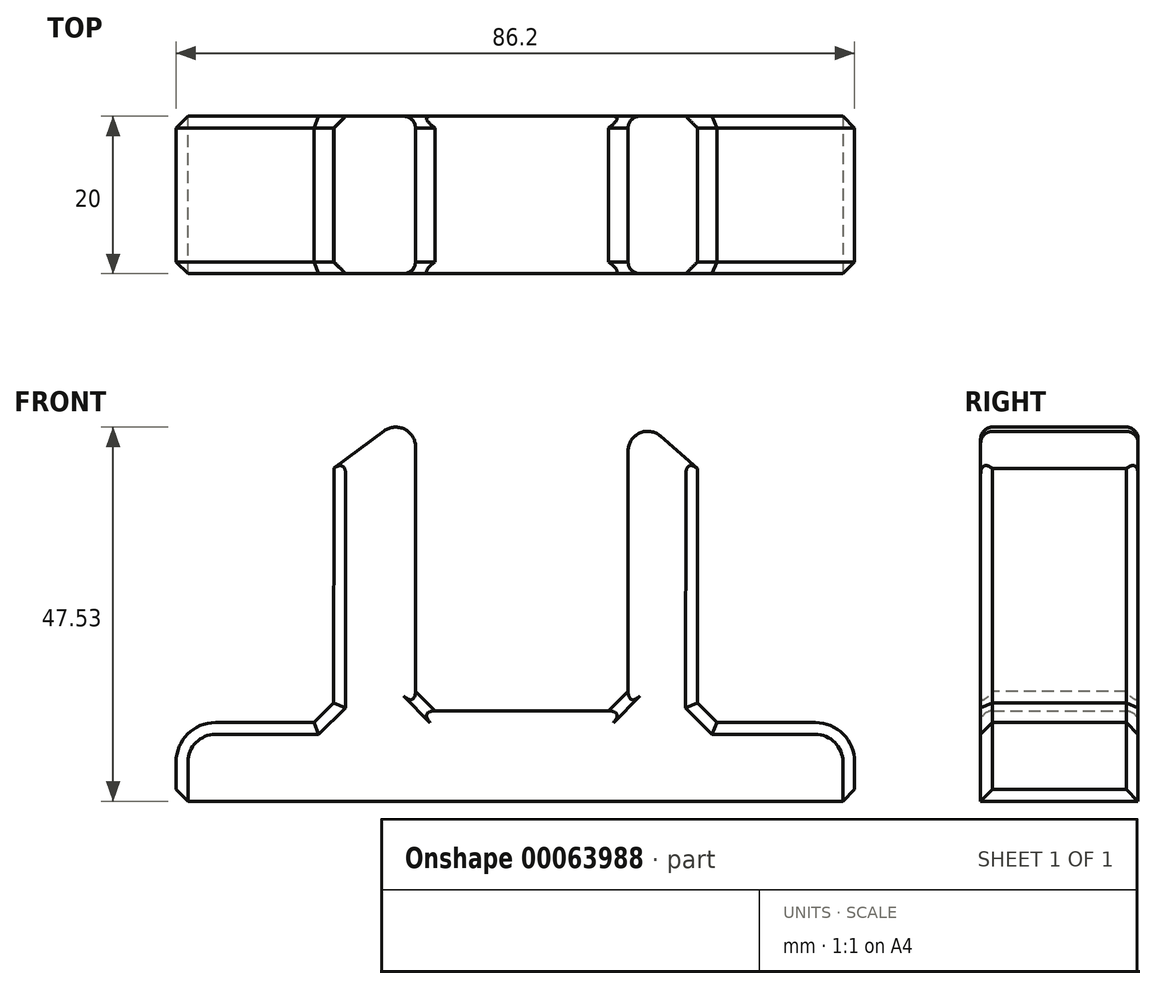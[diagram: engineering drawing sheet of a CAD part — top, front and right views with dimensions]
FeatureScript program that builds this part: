
annotation { "Feature Type Name" : "Feature", "Feature Type Description" : "" }
export const myFeature = defineFeature(function(context is Context, id is Id, definition is map)
    precondition{}
    {
        {
            var Q0;
            Q0=qCreatedBy(makeId("Front.planeOp"),FACE);
            var sketch = newSketch(context, id + "F0", { "sketchPlane" : qUnion([Q0])});
            skLineSegment(sketch, "E0.rect.bottom", {"start": v(43.1, 0) * mm, "end": v(-43.1, 0) * mm});
            skLineSegment(sketch, "E0.rect.top", {"start": v(43.1, 10) * mm, "end": v(23.1, 10) * mm});
            skLineSegment(sketch, "E0.rect.left", {"start": v(43.1, 0) * mm, "end": v(43.1, 10) * mm});
            skLineSegment(sketch, "E0.rect.right", {"start": v(-43.1, 0) * mm, "end": v(-43.1, 10) * mm});
            skPoint(sketch, "E0.rect.middle", {"position": v(0, 5) * mm});
            skLineSegment(sketch, "E1.left", {"start": v(-23.06, 42.34) * mm, "end": v(-23.1, 10) * mm});
            skLineSegment(sketch, "E1.right", {"start": v(23.14, 42.27) * mm, "end": v(23.1, 10) * mm});
            skLineSegment(sketch, "E2", {"start": v(-12.7, 49.99) * mm, "end": v(-12.7, 11.49) * mm});
            skLineSegment(sketch, "E3", {"start": v(-12.7, 11.49) * mm, "end": v(14.3, 11.49) * mm});
            skLineSegment(sketch, "E4", {"start": v(14.3, 11.49) * mm, "end": v(14.3, 50.01) * mm});
            skLineSegment(sketch, "E5.trimOffspring", {"start": v(-23.1, 10) * mm, "end": v(-43.1, 10) * mm});
            skPoint(sketch, "E1.bottom.end.orphan", {"position": v(-12.7, 90.4) * mm});
            skPoint(sketch, "E6.trimOffspring.start.orphan", {"position": v(14.3, 90.4) * mm});
            skLineSegment(sketch, "E7", {"start": v(-12.7, 49.99) * mm, "end": v(-23.06, 42.34) * mm});
            skLineSegment(sketch, "E8", {"start": v(23.14, 42.27) * mm, "end": v(14.3, 50.01) * mm});
            skSolve(sketch);
        }
        {
            var Q0;
            Q0=makeQuery(id+"F0.imprint","IMPRINT",FACE,{"disambiguationData":[TD([[makeQuery(id+"F0.imprint","IMPRINT",EDGE,{"derivedFrom":sQuery(id+"F0.wireOp",EDGE,"E0.rect.bottom")}),-1.0]])]});
            extrude(context, id + "F1", {"entities" : qUnion([Q0]), "depth" : 20 * mm});
        }
        {
            var Q0;
            Q0=makeQuery(id+"F1.opExtrude","SWEPT_EDGE",EDGE,{"disambiguationData":[OSD([sQuery(id+"F0.wireOp",EDGE,"E0.rect.top"),sQuery(id+"F0.wireOp",EDGE,"E0.rect.left")])]});
            fillet(context, id + "F2", {"entities" : qUnion([Q0]), "radius" : 5 * mm, "tangentPropagation" : true, "allowEdgeOverflow" : false});
        }
        {
            var Q0;
            Q0=makeQuery(id+"F1.opExtrude","SWEPT_EDGE",EDGE,{"disambiguationData":[OSD([sQuery(id+"F0.wireOp",EDGE,"E0.rect.right"),sQuery(id+"F0.wireOp",EDGE,"E5.trimOffspring")])]});
            fillet(context, id + "F3", {"entities" : qUnion([Q0]), "radius" : 5 * mm, "tangentPropagation" : true, "allowEdgeOverflow" : false});
        }
        {
            var Q0;
            Q0=makeQuery(id+"F1.opExtrude","SWEPT_EDGE",EDGE,{"disambiguationData":[OSD([sQuery(id+"F0.wireOp",EDGE,"E1.left"),sQuery(id+"F0.wireOp",EDGE,"E5.trimOffspring")])]});
            var Q1;
            Q1=makeQuery(id+"F1.opExtrude","SWEPT_EDGE",EDGE,{"disambiguationData":[OSD([sQuery(id+"F0.wireOp",EDGE,"E0.rect.top"),sQuery(id+"F0.wireOp",EDGE,"E1.right")])]});
            chamfer(context, id + "F4", {"entities" : qUnion([Q0, Q1]), "width" : 2.5 * mm, "tangentPropagation" : true});
        }
        {
            var Q0;
            Q0=makeQuery(id+"F1.opExtrude","SWEPT_EDGE",EDGE,{"disambiguationData":[OSD([sQuery(id+"F0.wireOp",EDGE,"E0.rect.bottom"),sQuery(id+"F0.wireOp",EDGE,"E0.rect.right")])]});
            chamfer(context, id + "F5", {"entities" : qUnion([Q0]), "width" : 1.5 * mm, "tangentPropagation" : true});
        }
        {
            var Q0;
            Q0=makeQuery(id+"F1.opExtrude","SWEPT_EDGE",EDGE,{"disambiguationData":[OSD([sQuery(id+"F0.wireOp",EDGE,"E0.rect.bottom"),sQuery(id+"F0.wireOp",EDGE,"E0.rect.left")])]});
            chamfer(context, id + "F6", {"entities" : qUnion([Q0]), "width" : 1.5 * mm, "tangentPropagation" : true});
        }
        {
            var Q0;
            Q0=makeQuery(id+"F1.opExtrude","SWEPT_EDGE",EDGE,{"disambiguationData":[OSD([sQuery(id+"F0.wireOp",EDGE,"E2"),sQuery(id+"F0.wireOp",EDGE,"E3")])]});
            chamfer(context, id + "F7", {"entities" : qUnion([Q0]), "width" : 2.5 * mm, "tangentPropagation" : true});
        }
        {
            var Q0;
            Q0=makeQuery(id+"F1.opExtrude","SWEPT_EDGE",EDGE,{"disambiguationData":[OSD([sQuery(id+"F0.wireOp",EDGE,"E3"),sQuery(id+"F0.wireOp",EDGE,"E4")])]});
            chamfer(context, id + "F8", {"entities" : qUnion([Q0]), "width" : 2.5 * mm, "tangentPropagation" : true});
        }
        {
            var Q0;
            Q0=makeQuery(id+"F1.opExtrude","SWEPT_EDGE",EDGE,{"disambiguationData":[OSD([sQuery(id+"F0.wireOp",EDGE,"E2"),sQuery(id+"F0.wireOp",EDGE,"E7")])]});
            fillet(context, id + "F9", {"entities" : qUnion([Q0]), "radius" : 2.5 * mm, "tangentPropagation" : true, "allowEdgeOverflow" : false});
        }
        {
            var Q0;
            Q0=makeQuery(id+"F1.opExtrude","SWEPT_EDGE",EDGE,{"disambiguationData":[OSD([sQuery(id+"F0.wireOp",EDGE,"E4"),sQuery(id+"F0.wireOp",EDGE,"E8")])]});
            fillet(context, id + "F10", {"entities" : qUnion([Q0]), "radius" : 2.5 * mm, "tangentPropagation" : true, "allowEdgeOverflow" : false});
        }
        {
            var Q0;
            Q0=makeQuery(id+"F1.opExtrude","CAP_EDGE",EDGE,{"disambiguationData":[OSD([sQuery(id+"F0.wireOp",EDGE,"E1.left")])],"isStart":false});
            chamfer(context, id + "F11", {"entities" : qUnion([Q0]), "width" : 1.5 * mm, "tangentPropagation" : true});
        }
        {
            var Q0;
            Q0=makeQuery(id+"F1.opExtrude","CAP_EDGE",EDGE,{"disambiguationData":[OSD([sQuery(id+"F0.wireOp",EDGE,"E1.right")])],"isStart":true});
            var Q1;
            Q1=makeQuery(id+"F1.opExtrude","CAP_EDGE",EDGE,{"disambiguationData":[OSD([sQuery(id+"F0.wireOp",EDGE,"E1.left")])],"isStart":true});
            var Q2;
            Q2=makeQuery(id+"F1.opExtrude","CAP_EDGE",EDGE,{"disambiguationData":[OSD([sQuery(id+"F0.wireOp",EDGE,"E1.right")])],"isStart":false});
            chamfer(context, id + "F12", {"entities" : qUnion([Q0, Q1, Q2]), "width" : 1.5 * mm, "tangentPropagation" : true});
        }
        {
            var Q0;
            Q0=makeQuery(id+"F1.opExtrude","CAP_EDGE",EDGE,{"disambiguationData":[OSD([sQuery(id+"F0.wireOp",EDGE,"E2")])],"isStart":false});
            var Q1;
            Q1=makeQuery(id+"F1.opExtrude","CAP_EDGE",EDGE,{"disambiguationData":[OSD([sQuery(id+"F0.wireOp",EDGE,"E4")])],"isStart":false});
            fillet(context, id + "F13", {"entities" : qUnion([Q0, Q1]), "radius" : 1.5 * mm, "tangentPropagation" : true, "allowEdgeOverflow" : false});
        }
        {
            var Q0;
            {var subQ0=sQuery(id+"F0.wireOp",EDGE,"E1.right");var subQ1=sQuery(id+"F0.wireOp",EDGE,"E0.rect.top");Q0=makeQuery(id+"F4.opChamfer","BLEND_EDGE",EDGE,{"blendedFrom":[makeQuery(id+"F1.opExtrude","SWEPT_EDGE",EDGE,{"disambiguationData":[OSD([subQ1,subQ0])]}),makeQuery(id+"F1.opExtrude","CAP_FACE",FACE,{"disambiguationData":[OSD([sQuery(id+"F0.wireOp",EDGE,"E0.rect.bottom"),subQ1,sQuery(id+"F0.wireOp",EDGE,"E0.rect.left"),sQuery(id+"F0.wireOp",EDGE,"E0.rect.right"),sQuery(id+"F0.wireOp",EDGE,"E1.left"),subQ0,sQuery(id+"F0.wireOp",EDGE,"E2"),sQuery(id+"F0.wireOp",EDGE,"E3"),sQuery(id+"F0.wireOp",EDGE,"E4"),sQuery(id+"F0.wireOp",EDGE,"E5.trimOffspring"),sQuery(id+"F0.wireOp",EDGE,"E7"),sQuery(id+"F0.wireOp",EDGE,"E8")])],"isStart":false})],"blendedInto":[makeQuery(id+"F1.opExtrude","CAP_FACE",FACE,{"disambiguationData":[OSD([sQuery(id+"F0.wireOp",EDGE,"E0.rect.bottom"),subQ1,sQuery(id+"F0.wireOp",EDGE,"E0.rect.left"),sQuery(id+"F0.wireOp",EDGE,"E0.rect.right"),sQuery(id+"F0.wireOp",EDGE,"E1.left"),subQ0,sQuery(id+"F0.wireOp",EDGE,"E2"),sQuery(id+"F0.wireOp",EDGE,"E3"),sQuery(id+"F0.wireOp",EDGE,"E4"),sQuery(id+"F0.wireOp",EDGE,"E5.trimOffspring"),sQuery(id+"F0.wireOp",EDGE,"E7"),sQuery(id+"F0.wireOp",EDGE,"E8")])],"isStart":false})]});}
            chamfer(context, id + "F14", {"entities" : qUnion([Q0]), "width" : 1.5 * mm, "tangentPropagation" : true});
        }
        {
            var Q0;
            Q0=makeQuery(id+"F1.opExtrude","CAP_EDGE",EDGE,{"disambiguationData":[OSD([sQuery(id+"F0.wireOp",EDGE,"E0.rect.top")])],"isStart":false});
            var Q1;
            Q1=makeQuery(id+"F1.opExtrude","CAP_EDGE",EDGE,{"disambiguationData":[OSD([sQuery(id+"F0.wireOp",EDGE,"E0.rect.top")])],"isStart":true});
            var Q2;
            {var subQ0=sQuery(id+"F0.wireOp",EDGE,"E1.right");var subQ1=sQuery(id+"F0.wireOp",EDGE,"E0.rect.top");Q2=makeQuery(id+"F4.opChamfer","BLEND_EDGE",EDGE,{"blendedFrom":[makeQuery(id+"F1.opExtrude","SWEPT_EDGE",EDGE,{"disambiguationData":[OSD([subQ1,subQ0])]}),makeQuery(id+"F1.opExtrude","CAP_FACE",FACE,{"disambiguationData":[OSD([sQuery(id+"F0.wireOp",EDGE,"E0.rect.bottom"),subQ1,sQuery(id+"F0.wireOp",EDGE,"E0.rect.left"),sQuery(id+"F0.wireOp",EDGE,"E0.rect.right"),sQuery(id+"F0.wireOp",EDGE,"E1.left"),subQ0,sQuery(id+"F0.wireOp",EDGE,"E2"),sQuery(id+"F0.wireOp",EDGE,"E3"),sQuery(id+"F0.wireOp",EDGE,"E4"),sQuery(id+"F0.wireOp",EDGE,"E5.trimOffspring"),sQuery(id+"F0.wireOp",EDGE,"E7"),sQuery(id+"F0.wireOp",EDGE,"E8")])],"isStart":true})],"blendedInto":[makeQuery(id+"F1.opExtrude","CAP_FACE",FACE,{"disambiguationData":[OSD([sQuery(id+"F0.wireOp",EDGE,"E0.rect.bottom"),subQ1,sQuery(id+"F0.wireOp",EDGE,"E0.rect.left"),sQuery(id+"F0.wireOp",EDGE,"E0.rect.right"),sQuery(id+"F0.wireOp",EDGE,"E1.left"),subQ0,sQuery(id+"F0.wireOp",EDGE,"E2"),sQuery(id+"F0.wireOp",EDGE,"E3"),sQuery(id+"F0.wireOp",EDGE,"E4"),sQuery(id+"F0.wireOp",EDGE,"E5.trimOffspring"),sQuery(id+"F0.wireOp",EDGE,"E7"),sQuery(id+"F0.wireOp",EDGE,"E8")])],"isStart":true})]});}
            var Q3;
            {var subQ0=sQuery(id+"F0.wireOp",EDGE,"E4");var subQ1=sQuery(id+"F0.wireOp",EDGE,"E3");Q3=makeQuery(id+"F8.opChamfer","BLEND_EDGE",EDGE,{"blendedFrom":[makeQuery(id+"F1.opExtrude","SWEPT_EDGE",EDGE,{"disambiguationData":[OSD([subQ1,subQ0])]}),makeQuery(id+"F1.opExtrude","CAP_FACE",FACE,{"disambiguationData":[OSD([sQuery(id+"F0.wireOp",EDGE,"E0.rect.bottom"),sQuery(id+"F0.wireOp",EDGE,"E0.rect.top"),sQuery(id+"F0.wireOp",EDGE,"E0.rect.left"),sQuery(id+"F0.wireOp",EDGE,"E0.rect.right"),sQuery(id+"F0.wireOp",EDGE,"E1.left"),sQuery(id+"F0.wireOp",EDGE,"E1.right"),sQuery(id+"F0.wireOp",EDGE,"E2"),subQ1,subQ0,sQuery(id+"F0.wireOp",EDGE,"E5.trimOffspring"),sQuery(id+"F0.wireOp",EDGE,"E7"),sQuery(id+"F0.wireOp",EDGE,"E8")])],"isStart":false})],"blendedInto":[makeQuery(id+"F1.opExtrude","CAP_FACE",FACE,{"disambiguationData":[OSD([sQuery(id+"F0.wireOp",EDGE,"E0.rect.bottom"),sQuery(id+"F0.wireOp",EDGE,"E0.rect.top"),sQuery(id+"F0.wireOp",EDGE,"E0.rect.left"),sQuery(id+"F0.wireOp",EDGE,"E0.rect.right"),sQuery(id+"F0.wireOp",EDGE,"E1.left"),sQuery(id+"F0.wireOp",EDGE,"E1.right"),sQuery(id+"F0.wireOp",EDGE,"E2"),subQ1,subQ0,sQuery(id+"F0.wireOp",EDGE,"E5.trimOffspring"),sQuery(id+"F0.wireOp",EDGE,"E7"),sQuery(id+"F0.wireOp",EDGE,"E8")])],"isStart":false})]});}
            var Q4;
            {var subQ0=sQuery(id+"F0.wireOp",EDGE,"E3");var subQ1=sQuery(id+"F0.wireOp",EDGE,"E2");Q4=makeQuery(id+"F7.opChamfer","BLEND_EDGE",EDGE,{"blendedFrom":[makeQuery(id+"F1.opExtrude","SWEPT_EDGE",EDGE,{"disambiguationData":[OSD([subQ1,subQ0])]}),makeQuery(id+"F1.opExtrude","CAP_FACE",FACE,{"disambiguationData":[OSD([sQuery(id+"F0.wireOp",EDGE,"E0.rect.bottom"),sQuery(id+"F0.wireOp",EDGE,"E0.rect.top"),sQuery(id+"F0.wireOp",EDGE,"E0.rect.left"),sQuery(id+"F0.wireOp",EDGE,"E0.rect.right"),sQuery(id+"F0.wireOp",EDGE,"E1.left"),sQuery(id+"F0.wireOp",EDGE,"E1.right"),subQ1,subQ0,sQuery(id+"F0.wireOp",EDGE,"E4"),sQuery(id+"F0.wireOp",EDGE,"E5.trimOffspring"),sQuery(id+"F0.wireOp",EDGE,"E7"),sQuery(id+"F0.wireOp",EDGE,"E8")])],"isStart":false})],"blendedInto":[makeQuery(id+"F1.opExtrude","CAP_FACE",FACE,{"disambiguationData":[OSD([sQuery(id+"F0.wireOp",EDGE,"E0.rect.bottom"),sQuery(id+"F0.wireOp",EDGE,"E0.rect.top"),sQuery(id+"F0.wireOp",EDGE,"E0.rect.left"),sQuery(id+"F0.wireOp",EDGE,"E0.rect.right"),sQuery(id+"F0.wireOp",EDGE,"E1.left"),sQuery(id+"F0.wireOp",EDGE,"E1.right"),subQ1,subQ0,sQuery(id+"F0.wireOp",EDGE,"E4"),sQuery(id+"F0.wireOp",EDGE,"E5.trimOffspring"),sQuery(id+"F0.wireOp",EDGE,"E7"),sQuery(id+"F0.wireOp",EDGE,"E8")])],"isStart":false})]});}
            var Q5;
            {var subQ0=sQuery(id+"F0.wireOp",EDGE,"E5.trimOffspring");var subQ1=sQuery(id+"F0.wireOp",EDGE,"E1.left");Q5=makeQuery(id+"F4.opChamfer","BLEND_EDGE",EDGE,{"blendedFrom":[makeQuery(id+"F1.opExtrude","SWEPT_EDGE",EDGE,{"disambiguationData":[OSD([subQ1,subQ0])]}),makeQuery(id+"F1.opExtrude","CAP_FACE",FACE,{"disambiguationData":[OSD([sQuery(id+"F0.wireOp",EDGE,"E0.rect.bottom"),sQuery(id+"F0.wireOp",EDGE,"E0.rect.top"),sQuery(id+"F0.wireOp",EDGE,"E0.rect.left"),sQuery(id+"F0.wireOp",EDGE,"E0.rect.right"),subQ1,sQuery(id+"F0.wireOp",EDGE,"E1.right"),sQuery(id+"F0.wireOp",EDGE,"E2"),sQuery(id+"F0.wireOp",EDGE,"E3"),sQuery(id+"F0.wireOp",EDGE,"E4"),subQ0,sQuery(id+"F0.wireOp",EDGE,"E7"),sQuery(id+"F0.wireOp",EDGE,"E8")])],"isStart":false})],"blendedInto":[makeQuery(id+"F1.opExtrude","CAP_FACE",FACE,{"disambiguationData":[OSD([sQuery(id+"F0.wireOp",EDGE,"E0.rect.bottom"),sQuery(id+"F0.wireOp",EDGE,"E0.rect.top"),sQuery(id+"F0.wireOp",EDGE,"E0.rect.left"),sQuery(id+"F0.wireOp",EDGE,"E0.rect.right"),subQ1,sQuery(id+"F0.wireOp",EDGE,"E1.right"),sQuery(id+"F0.wireOp",EDGE,"E2"),sQuery(id+"F0.wireOp",EDGE,"E3"),sQuery(id+"F0.wireOp",EDGE,"E4"),subQ0,sQuery(id+"F0.wireOp",EDGE,"E7"),sQuery(id+"F0.wireOp",EDGE,"E8")])],"isStart":false})]});}
            var Q6;
            Q6=makeQuery(id+"F1.opExtrude","CAP_EDGE",EDGE,{"disambiguationData":[OSD([sQuery(id+"F0.wireOp",EDGE,"E5.trimOffspring")])],"isStart":false});
            var Q7;
            {var subQ0=sQuery(id+"F0.wireOp",EDGE,"E4");var subQ1=sQuery(id+"F0.wireOp",EDGE,"E3");Q7=makeQuery(id+"F8.opChamfer","BLEND_EDGE",EDGE,{"blendedFrom":[makeQuery(id+"F1.opExtrude","SWEPT_EDGE",EDGE,{"disambiguationData":[OSD([subQ1,subQ0])]}),makeQuery(id+"F1.opExtrude","CAP_FACE",FACE,{"disambiguationData":[OSD([sQuery(id+"F0.wireOp",EDGE,"E0.rect.bottom"),sQuery(id+"F0.wireOp",EDGE,"E0.rect.top"),sQuery(id+"F0.wireOp",EDGE,"E0.rect.left"),sQuery(id+"F0.wireOp",EDGE,"E0.rect.right"),sQuery(id+"F0.wireOp",EDGE,"E1.left"),sQuery(id+"F0.wireOp",EDGE,"E1.right"),sQuery(id+"F0.wireOp",EDGE,"E2"),subQ1,subQ0,sQuery(id+"F0.wireOp",EDGE,"E5.trimOffspring"),sQuery(id+"F0.wireOp",EDGE,"E7"),sQuery(id+"F0.wireOp",EDGE,"E8")])],"isStart":true})],"blendedInto":[makeQuery(id+"F1.opExtrude","CAP_FACE",FACE,{"disambiguationData":[OSD([sQuery(id+"F0.wireOp",EDGE,"E0.rect.bottom"),sQuery(id+"F0.wireOp",EDGE,"E0.rect.top"),sQuery(id+"F0.wireOp",EDGE,"E0.rect.left"),sQuery(id+"F0.wireOp",EDGE,"E0.rect.right"),sQuery(id+"F0.wireOp",EDGE,"E1.left"),sQuery(id+"F0.wireOp",EDGE,"E1.right"),sQuery(id+"F0.wireOp",EDGE,"E2"),subQ1,subQ0,sQuery(id+"F0.wireOp",EDGE,"E5.trimOffspring"),sQuery(id+"F0.wireOp",EDGE,"E7"),sQuery(id+"F0.wireOp",EDGE,"E8")])],"isStart":true})]});}
            var Q8;
            {var subQ0=sQuery(id+"F0.wireOp",EDGE,"E3");var subQ1=sQuery(id+"F0.wireOp",EDGE,"E2");Q8=makeQuery(id+"F7.opChamfer","BLEND_EDGE",EDGE,{"blendedFrom":[makeQuery(id+"F1.opExtrude","SWEPT_EDGE",EDGE,{"disambiguationData":[OSD([subQ1,subQ0])]}),makeQuery(id+"F1.opExtrude","CAP_FACE",FACE,{"disambiguationData":[OSD([sQuery(id+"F0.wireOp",EDGE,"E0.rect.bottom"),sQuery(id+"F0.wireOp",EDGE,"E0.rect.top"),sQuery(id+"F0.wireOp",EDGE,"E0.rect.left"),sQuery(id+"F0.wireOp",EDGE,"E0.rect.right"),sQuery(id+"F0.wireOp",EDGE,"E1.left"),sQuery(id+"F0.wireOp",EDGE,"E1.right"),subQ1,subQ0,sQuery(id+"F0.wireOp",EDGE,"E4"),sQuery(id+"F0.wireOp",EDGE,"E5.trimOffspring"),sQuery(id+"F0.wireOp",EDGE,"E7"),sQuery(id+"F0.wireOp",EDGE,"E8")])],"isStart":true})],"blendedInto":[makeQuery(id+"F1.opExtrude","CAP_FACE",FACE,{"disambiguationData":[OSD([sQuery(id+"F0.wireOp",EDGE,"E0.rect.bottom"),sQuery(id+"F0.wireOp",EDGE,"E0.rect.top"),sQuery(id+"F0.wireOp",EDGE,"E0.rect.left"),sQuery(id+"F0.wireOp",EDGE,"E0.rect.right"),sQuery(id+"F0.wireOp",EDGE,"E1.left"),sQuery(id+"F0.wireOp",EDGE,"E1.right"),subQ1,subQ0,sQuery(id+"F0.wireOp",EDGE,"E4"),sQuery(id+"F0.wireOp",EDGE,"E5.trimOffspring"),sQuery(id+"F0.wireOp",EDGE,"E7"),sQuery(id+"F0.wireOp",EDGE,"E8")])],"isStart":true})]});}
            var Q9;
            {var subQ0=sQuery(id+"F0.wireOp",EDGE,"E5.trimOffspring");var subQ1=sQuery(id+"F0.wireOp",EDGE,"E1.left");Q9=makeQuery(id+"F4.opChamfer","BLEND_EDGE",EDGE,{"blendedFrom":[makeQuery(id+"F1.opExtrude","SWEPT_EDGE",EDGE,{"disambiguationData":[OSD([subQ1,subQ0])]}),makeQuery(id+"F1.opExtrude","CAP_FACE",FACE,{"disambiguationData":[OSD([sQuery(id+"F0.wireOp",EDGE,"E0.rect.bottom"),sQuery(id+"F0.wireOp",EDGE,"E0.rect.top"),sQuery(id+"F0.wireOp",EDGE,"E0.rect.left"),sQuery(id+"F0.wireOp",EDGE,"E0.rect.right"),subQ1,sQuery(id+"F0.wireOp",EDGE,"E1.right"),sQuery(id+"F0.wireOp",EDGE,"E2"),sQuery(id+"F0.wireOp",EDGE,"E3"),sQuery(id+"F0.wireOp",EDGE,"E4"),subQ0,sQuery(id+"F0.wireOp",EDGE,"E7"),sQuery(id+"F0.wireOp",EDGE,"E8")])],"isStart":true})],"blendedInto":[makeQuery(id+"F1.opExtrude","CAP_FACE",FACE,{"disambiguationData":[OSD([sQuery(id+"F0.wireOp",EDGE,"E0.rect.bottom"),sQuery(id+"F0.wireOp",EDGE,"E0.rect.top"),sQuery(id+"F0.wireOp",EDGE,"E0.rect.left"),sQuery(id+"F0.wireOp",EDGE,"E0.rect.right"),subQ1,sQuery(id+"F0.wireOp",EDGE,"E1.right"),sQuery(id+"F0.wireOp",EDGE,"E2"),sQuery(id+"F0.wireOp",EDGE,"E3"),sQuery(id+"F0.wireOp",EDGE,"E4"),subQ0,sQuery(id+"F0.wireOp",EDGE,"E7"),sQuery(id+"F0.wireOp",EDGE,"E8")])],"isStart":true})]});}
            var Q10;
            Q10=makeQuery(id+"F1.opExtrude","CAP_EDGE",EDGE,{"disambiguationData":[OSD([sQuery(id+"F0.wireOp",EDGE,"E5.trimOffspring")])],"isStart":true});
            chamfer(context, id + "F15", {"entities" : qUnion([Q0, Q1, Q2, Q3, Q4, Q5, Q6, Q7, Q8, Q9, Q10]), "width" : 1.5 * mm, "tangentPropagation" : true});
        }
        {
            var Q0;
            Q0=makeQuery(id+"F1.opExtrude","CAP_EDGE",EDGE,{"disambiguationData":[OSD([sQuery(id+"F0.wireOp",EDGE,"E8")])],"isStart":true});
            var Q1;
            Q1=makeQuery(id+"F1.opExtrude","CAP_EDGE",EDGE,{"disambiguationData":[OSD([sQuery(id+"F0.wireOp",EDGE,"E7")])],"isStart":true});
            fillet(context, id + "F16", {"entities" : qUnion([Q0, Q1]), "radius" : 1.5 * mm, "tangentPropagation" : true, "allowEdgeOverflow" : false});
        }
        {
            var Q0;
            Q0=makeQuery(id+"F1.opExtrude","CAP_EDGE",EDGE,{"disambiguationData":[OSD([sQuery(id+"F0.wireOp",EDGE,"E3")])],"isStart":false});
            var Q1;
            Q1=makeQuery(id+"F1.opExtrude","CAP_EDGE",EDGE,{"disambiguationData":[OSD([sQuery(id+"F0.wireOp",EDGE,"E3")])],"isStart":true});
            fillet(context, id + "F17", {"entities" : qUnion([Q0, Q1]), "radius" : 1.5 * mm, "tangentPropagation" : true, "allowEdgeOverflow" : false});
        }
        {
            var Q0;
            Q0=makeQuery(id+"F1.opExtrude","SWEPT_BODY",BODY,{"disambiguationData":[OSD([sQuery(id+"F0.wireOp",EDGE,"E0.rect.bottom"),sQuery(id+"F0.wireOp",EDGE,"E0.rect.top"),sQuery(id+"F0.wireOp",EDGE,"E0.rect.left"),sQuery(id+"F0.wireOp",EDGE,"E0.rect.right"),sQuery(id+"F0.wireOp",EDGE,"E1.left"),sQuery(id+"F0.wireOp",EDGE,"E1.right"),sQuery(id+"F0.wireOp",EDGE,"E2"),sQuery(id+"F0.wireOp",EDGE,"E3"),sQuery(id+"F0.wireOp",EDGE,"E4"),sQuery(id+"F0.wireOp",EDGE,"E5.trimOffspring"),sQuery(id+"F0.wireOp",EDGE,"E7"),sQuery(id+"F0.wireOp",EDGE,"E8")])]});
            transform(context, id + "F18", {"entities" : qUnion([Q0]), "transformType" : TransformType.TRANSLATION_3D, "dx" : 0 * mm, "dy" : 0 * mm, "dz" : 0 * mm, "makeCopy" : true});
        }
    });
